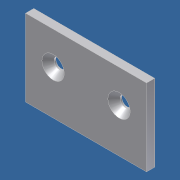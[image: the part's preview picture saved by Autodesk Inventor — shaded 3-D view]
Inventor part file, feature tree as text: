
AUTODESK INVENTOR PART (.ipt)
format: ipt  version: unknown  size: 177,664 bytes
history: native  units: in
note: dims shown in document units (in); Inventor stores cm internally (conversion verified against a paired STEP export)
features: sketch x2, extrude x1, hole x1
ambient origin geometry x8: Origin, YZ Plane, XZ Plane, XY Plane, X Axis, Y Axis, Z Axis, Center Point
bodies: Solid1 (feature_tree)
feature tree (4):
  extrude  "Extrusion1"  Depth=2.75in
  hole  "Hole1"  [1 undecoded]
  sketch  "Sketch1"  dims[d0=1.75in d1=2.75in]
  sketch  "Sketch2"  dims[d2=0.187in d3=0.0in d4=0.625in d5=1.5in d6=1.0in d7=0.25in d8=0.75in d9=0.507in d10=0.25in d11=0.5635in d12=0.75in d13=0.8108in]
note: 1 required parameter value undecoded (feature->parameter linkage not recoverable at this tier; creation-order binding heuristic only, values carry confidence <= 0.55)
